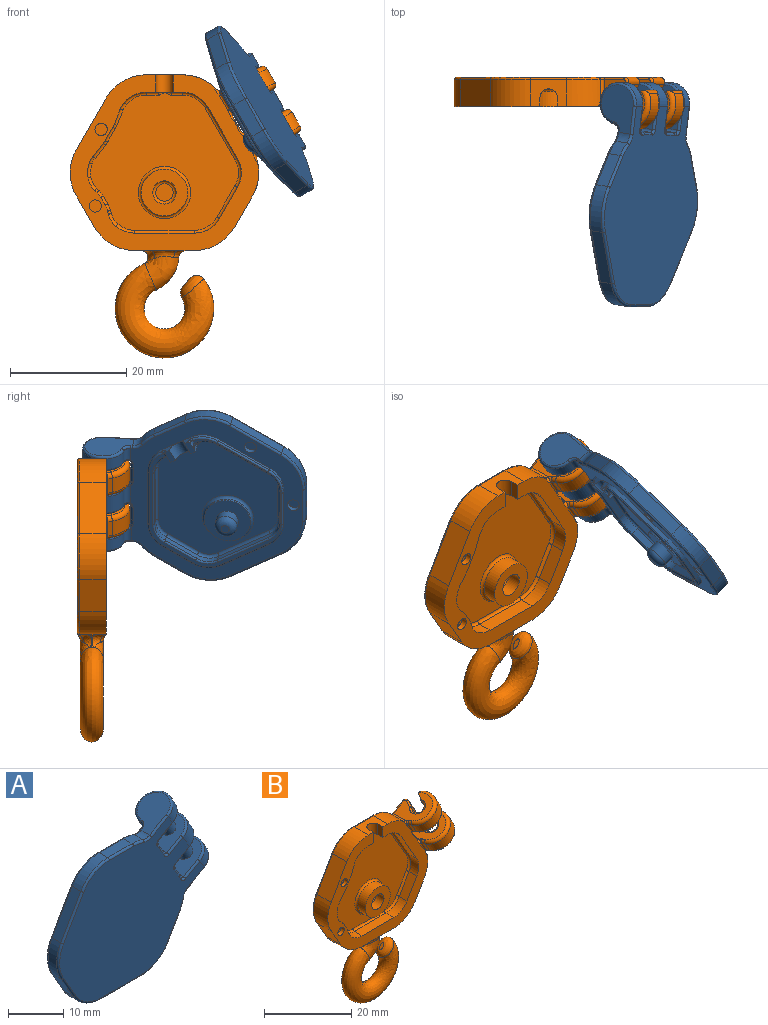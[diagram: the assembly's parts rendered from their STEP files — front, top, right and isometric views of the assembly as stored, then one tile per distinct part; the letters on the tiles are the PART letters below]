
ASSEMBLY  parts=2 mates=1
PART A: 201 faces, bbox 41.9x8.3x35.3 mm
  f0: plane 3.11x1.5mm, normal (0,0,1), area 2.3mm2, adj f20,f39,f76,f77,f115,f116
  f1: plane 22.85x20.65mm, normal (0,1,0), area 295.9mm2, adj f79,f82,f84,f85,f86,f87,f88,f89
  f2: plane 1.2x0.11mm, normal (0,0,-1), area 0.1mm2, adj f47,f80,f96,f130
  f3: cylinder r=8mm len=2.65mm, axis (0,1,0), area 6.2mm2, adj f10,f68,f163,f170
  f4: cylinder r=8mm len=2.1mm, axis (0,1,0), area 2mm2, adj f12,f65,f134,f180
  f5: cylinder r=1.5mm len=5.48mm, axis (0.5,0,-0.87), area 43.4mm2, adj f21,f28
  f6: plane 2.26x2.1mm, normal (0.87,0,0.5), area 5.5mm2, adj f11,f66,f138,f194
  f7: cylinder r=8mm len=6.93mm, axis (0,1,0), area 18.4mm2, adj f8,f18,f155,f162
  f8: plane 10.23x2.2mm, normal (0,0,-1), area 22.5mm2, adj f7,f9,f157,f164
  f9: cylinder r=8mm len=6.93mm, axis (0,1,0), area 18.4mm2, adj f8,f10,f159,f166
  f10: plane 5.39x3.11mm, normal (0.87,0,-0.5), area 13.7mm2, adj f3,f9,f161,f168
  f11: cylinder r=8mm len=2.1mm, axis (0,1,0), area 2mm2, adj f6,f67,f132,f195
  f12: plane 2.26x2.1mm, normal (0.87,0,0.5), area 5.5mm2, adj f4,f64,f136,f181
  f13: cylinder r=8mm len=2.78mm, axis (0,1,0), area 6.2mm2, adj f14,f69,f143,f150
  f14: plane 6.23x2.2mm, normal (0,0,1), area 13.7mm2, adj f13,f15,f145,f152
  f15: cylinder r=8mm len=6.93mm, axis (0,1,0), area 18.4mm2, adj f14,f16,f147,f154
  f16: plane 8.86x5.11mm, normal (-0.87,0,0.5), area 22.5mm2, adj f15,f17,f149,f156
  f17: cylinder r=8mm len=8mm, axis (0,1,0), area 18.4mm2, adj f16,f18,f151,f158
  f18: plane 5.39x3.11mm, normal (-0.87,0,-0.5), area 13.7mm2, adj f7,f17,f153,f160
  f19: plane 36.96x31.6mm, normal (0,-1,0), area 769.8mm2, adj f24,f27,f61,f140,f141,f143,f145,f147
  f20: plane 33.32x29.92mm, normal (0,1,0), area 251.9mm2, adj f0,f23,f26,f30,f31,f32,f33,f34
  f21: plane 6.4x6.34mm, normal (-0.5,0,0.87), area 29.7mm2, adj f5,f136,f137,f183,f184,f185
  f22: plane 6.4x6.34mm, normal (0.5,0,-0.87), area 29.7mm2, adj f25,f138,f139,f190,f191,f192
  f23: cylinder r=1.02mm len=3.53mm, axis (0.5,0,-0.87), area 4.9mm2, adj f20,f24,f185,f186,f189,f190
  f24: cylinder r=3.6mm len=7.82mm, axis (0.5,0,-0.87), area 53.2mm2, adj f19,f23,f184,f191
  f25: cylinder r=1.5mm len=5.48mm, axis (0.5,0,-0.87), area 43.4mm2, adj f22,f62
  f26: cylinder r=1.02mm len=2.42mm, axis (0.5,0,-0.87), area 3.2mm2, adj f20,f27,f144,f175,f176
  f27: cylinder r=3.6mm len=7.27mm, axis (0.5,0,-0.87), area 34.9mm2, adj f19,f26,f142,f177
  f28: plane 6.4x6.38mm, normal (0.5,0,-0.87), area 29.8mm2, adj f5,f134,f135,f176,f177,f178
  f29: plane 7.02x6.4mm, normal (-0.5,0,0.87), area 38.5mm2, adj f69,f140,f142,f144,f146
  f30: plane 9.65x0.7mm, normal (0,0,-1), area 6.8mm2, adj f20,f36,f41,f109
  f31: plane 5.39x3.11mm, normal (0.87,0,-0.5), area 4.4mm2, adj f20,f40,f41,f111
  f32: plane 8.86x5.11mm, normal (0.87,0,0.5), area 7.2mm2, adj f20,f39,f40,f113
  f33: plane 2.54x1.5mm, normal (0,0,1), area 1.9mm2, adj f20,f38,f76,f78,f102
  f34: plane 8.86x5.11mm, normal (-0.87,0,0.5), area 7.2mm2, adj f20,f37,f38,f105
  f35: plane 5.39x3.11mm, normal (-0.87,0,-0.5), area 4.4mm2, adj f20,f36,f37,f107
  f36: cylinder r=4.9mm len=4.24mm, axis (0,-1,0), area 3.6mm2, adj f20,f30,f35,f108
  f37: cylinder r=4.9mm len=4.9mm, axis (0,-1,0), area 3.6mm2, adj f20,f34,f35,f106
  f38: cylinder r=4.9mm len=4.24mm, axis (0,-1,0), area 3.6mm2, adj f20,f33,f34,f103,f104
  f39: cylinder r=4.9mm len=4.24mm, axis (0,-1,0), area 3.6mm2, adj f0,f20,f32,f114
  f40: cylinder r=4.9mm len=4.9mm, axis (0,-1,0), area 3.6mm2, adj f20,f31,f32,f112
  f41: cylinder r=4.9mm len=4.24mm, axis (0,-1,0), area 3.6mm2, adj f20,f30,f31,f110
  f42: plane 10.23x1.2mm, normal (0,0,1), area 12.3mm2, adj f43,f53,f90,f124
  f43: cylinder r=3.7mm len=3.2mm, axis (0,-1,0), area 4.6mm2, adj f42,f44,f91,f125
  f44: plane 5.39x3.11mm, normal (-0.87,0,0.5), area 7.5mm2, adj f43,f45,f92,f126
  f45: cylinder r=3.7mm len=3.7mm, axis (0,-1,0), area 4.6mm2, adj f44,f46,f93,f127
  f46: plane 8.86x5.11mm, normal (-0.87,0,-0.5), area 12.3mm2, adj f45,f47,f94,f128
  f47: cylinder r=3.7mm len=3.2mm, axis (0,-1,0), area 4.6mm2, adj f2,f46,f95,f129
  f48: plane 1.2x0.11mm, normal (0,0,-1), area 0.1mm2, adj f49,f81,f84,f118
  f49: cylinder r=3.7mm len=3.2mm, axis (0,-1,0), area 4.6mm2, adj f48,f50,f85,f119
  f50: plane 8.86x5.11mm, normal (0.87,0,-0.5), area 12.3mm2, adj f49,f51,f86,f120
  f51: cylinder r=3.7mm len=3.7mm, axis (0,-1,0), area 4.6mm2, adj f50,f52,f87,f121
  f52: plane 5.39x3.11mm, normal (0.87,0,0.5), area 7.5mm2, adj f51,f53,f88,f122
  f53: cylinder r=3.7mm len=3.2mm, axis (0,-1,0), area 4.6mm2, adj f42,f52,f89,f123
  f54: plane 25.08x23.45mm, normal (0,1,0), area 28.7mm2, adj f100,f101,f104,f105,f106,f107,f108,f109
  f55: cylinder r=4mm len=8mm, axis (0,-1,0), area 12.6mm2, adj f56,f99
  f56: plane 8x8mm, normal (0,1,0), area 38.9mm2, adj f55,f59
  f57: plane 1.4x1.4mm, normal (0,1,0), area 1.5mm2, adj f58
  f58: torus R=0.7mm, axis (0,1,0), area 17.3mm2, adj f57,f59
  f59: cylinder r=1.9mm len=3.8mm, axis (0,-1,0), area 21.5mm2, adj f56,f58
  f60: cylinder r=1.02mm len=2.61mm, axis (-0.5,0,0.87), area 3.5mm2, adj f20,f61,f171,f199,f200
  f61: cylinder r=3.6mm len=7.27mm, axis (-0.5,0,0.87), area 35mm2, adj f19,f60,f169,f198
  f62: plane 6.4x6.38mm, normal (-0.5,0,0.87), area 29.8mm2, adj f25,f132,f133,f197,f198,f199
  f63: plane 7.02x6.4mm, normal (0.5,0,-0.87), area 38.5mm2, adj f68,f167,f169,f171,f173
  f64: cylinder r=0.5mm len=2.51mm, axis (0.5,0,-0.87), area 2.1mm2, adj f12,f20,f65,f137
  f65: torus R=7.5mm, axis (0,1,0), area 0.8mm2, adj f4,f20,f64,f135
  f66: cylinder r=0.5mm len=2.51mm, axis (0.5,0,-0.87), area 2.1mm2, adj f6,f20,f67,f139
  f67: torus R=7.5mm, axis (0,1,0), area 0.8mm2, adj f11,f20,f66,f133
  f68: cylinder r=2mm len=2.2mm, axis (0,1,0), area 3.9mm2, adj f3,f63,f165,f172
  f69: cylinder r=2mm len=2.2mm, axis (0,1,0), area 3.9mm2, adj f13,f29,f141,f148
  f70: cylinder r=1.05mm len=2.1mm, axis (0,1,0), area 6.9mm2, adj f20,f71
  f71: plane 2.1x2.1mm, normal (0,1,0), area 3.5mm2, adj f70
  f72: cylinder r=1.05mm len=2.1mm, axis (0,1,0), area 6.9mm2, adj f20,f73
  f73: plane 2.1x2.1mm, normal (0,1,0), area 3.5mm2, adj f72
  f74: plane 2x0.5mm, normal (1,0,0), area 1mm2, adj f77,f79,f80,f98
  f75: plane 2x0.5mm, normal (-1,0,0), area 1mm2, adj f78,f79,f81,f82
  f76: cylinder r=1.5mm len=3mm, axis (0,0,-1), area 10.4mm2, adj f0,f33,f77,f78,f79
  f77: plane 2.2x1mm, normal (0,1,0), area 2.2mm2, adj f0,f74,f76,f79,f100,f116
  f78: plane 2.2x1mm, normal (0,1,0), area 2.2mm2, adj f33,f75,f76,f79,f101,f102
  f79: plane 6x2.5mm, normal (0,0,-1), area 9.1mm2, adj f1,f74,f75,f76,f77,f78,f82,f98
  f80: cylinder r=0.5mm len=2mm, axis (0,1,0), area 1.3mm2, adj f2,f74,f97,f131
  f81: cylinder r=0.5mm len=2mm, axis (0,-1,0), area 1.3mm2, adj f48,f75,f83,f117
  f82: cylinder r=0.5mm len=0.5mm, axis (0,0,-1), area 0.4mm2, adj f1,f75,f79,f83
  f83: sphere r=0.5mm, area 0.5mm2, adj f81,f82,f84
  f84: cylinder r=0.5mm len=0.5mm, axis (1,0,0), area 0.1mm2, adj f1,f48,f83,f85
  f85: torus R=3.2mm, axis (0,-1,0), area 2.9mm2, adj f1,f49,f84,f86
  f86: cylinder r=0.5mm len=9.11mm, axis (0.5,0,0.87), area 8mm2, adj f1,f50,f85,f87
  f87: torus R=3.2mm, axis (0,-1,0), area 2.9mm2, adj f1,f51,f86,f88
  f88: cylinder r=0.5mm len=5.64mm, axis (-0.5,0,0.87), area 4.9mm2, adj f1,f52,f87,f89
  f89: torus R=3.2mm, axis (0,-1,0), area 2.9mm2, adj f1,f53,f88,f90
  f90: cylinder r=0.5mm len=10.23mm, axis (-1,0,0), area 8mm2, adj f1,f42,f89,f91
  f91: torus R=3.2mm, axis (0,-1,0), area 2.9mm2, adj f1,f43,f90,f92
  f92: cylinder r=0.5mm len=5.64mm, axis (-0.5,0,-0.87), area 4.9mm2, adj f1,f44,f91,f93
  f93: torus R=3.2mm, axis (0,-1,0), area 2.9mm2, adj f1,f45,f92,f94
  f94: cylinder r=0.5mm len=9.11mm, axis (0.5,0,-0.87), area 8mm2, adj f1,f46,f93,f95
  f95: torus R=3.2mm, axis (0,-1,0), area 2.9mm2, adj f1,f47,f94,f96
  f96: cylinder r=0.5mm len=0.5mm, axis (1,0,0), area 0.1mm2, adj f1,f2,f95,f97
  f97: sphere r=0.5mm, area 0.4mm2, adj f80,f96,f98
  f98: cylinder r=0.5mm len=0.5mm, axis (0,0,-1), area 0.4mm2, adj f1,f74,f79,f97
  f99: torus R=4.5mm, axis (0,-1,0), area 20.6mm2, adj f1,f55
  f100: cylinder r=0.5mm len=1.4mm, axis (0,0,1), area 0.8mm2, adj f54,f77,f116,f131
  f101: cylinder r=0.5mm len=1.4mm, axis (0,0,-1), area 0.7mm2, adj f54,f78,f102,f103,f117
  f102: torus R=0.8mm, axis (0,0,1), area 0.3mm2, adj f33,f78,f101,f103
  f103: bspline ~0.69x0.47mm, area 0.2mm2, adj f38,f101,f102,f104
  f104: torus R=4.6mm, axis (0,1,0), area 2.1mm2, adj f38,f54,f103,f105
  f105: cylinder r=0.3mm len=9.01mm, axis (-0.5,0,-0.87), area 4.8mm2, adj f34,f54,f104,f106
  f106: torus R=4.6mm, axis (0,1,0), area 2.4mm2, adj f37,f54,f105,f107
  f107: cylinder r=0.3mm len=5.54mm, axis (0.5,0,-0.87), area 2.9mm2, adj f35,f54,f106,f108
  f108: torus R=4.6mm, axis (0,1,0), area 2.4mm2, adj f36,f54,f107,f109
  f109: cylinder r=0.3mm len=9.65mm, axis (1,0,0), area 4.5mm2, adj f30,f54,f108,f110
  f110: torus R=4.6mm, axis (0,1,0), area 2.4mm2, adj f41,f54,f109,f111
  f111: cylinder r=0.3mm len=5.54mm, axis (0.5,0,0.87), area 2.9mm2, adj f31,f54,f110,f112
  f112: torus R=4.6mm, axis (0,1,0), area 2.4mm2, adj f40,f54,f111,f113
  f113: cylinder r=0.3mm len=9.01mm, axis (-0.5,0,0.87), area 4.8mm2, adj f32,f54,f112,f114
  f114: torus R=4.6mm, axis (0,1,0), area 2.4mm2, adj f39,f54,f113,f115
  f115: cylinder r=0.3mm len=0.3mm, axis (-1,0,0), area 0.1mm2, adj f0,f54,f114,f116
  f116: torus R=0.8mm, axis (0,0,1), area 0.5mm2, adj f0,f77,f100,f115
  f117: bspline ~0.8x0.8mm, area 0.2mm2, adj f81,f101,f118
  f118: cylinder r=0.3mm len=0.3mm, axis (1,0,0), area 0.1mm2, adj f48,f54,f117,f119
  f119: torus R=4mm, axis (0,1,0), area 1.9mm2, adj f49,f54,f118,f120
  f120: cylinder r=0.3mm len=9.01mm, axis (0.5,0,0.87), area 4.8mm2, adj f50,f54,f119,f121
  f121: torus R=4mm, axis (0,1,0), area 1.9mm2, adj f51,f54,f120,f122
  f122: cylinder r=0.3mm len=5.54mm, axis (-0.5,0,0.87), area 2.9mm2, adj f52,f54,f121,f123
  f123: torus R=4mm, axis (0,1,0), area 1.9mm2, adj f53,f54,f122,f124
  f124: cylinder r=0.3mm len=10.23mm, axis (-1,0,0), area 4.8mm2, adj f42,f54,f123,f125
  f125: torus R=4mm, axis (0,1,0), area 1.9mm2, adj f43,f54,f124,f126
  f126: cylinder r=0.3mm len=5.54mm, axis (-0.5,0,-0.87), area 2.9mm2, adj f44,f54,f125,f127
  f127: torus R=4mm, axis (0,1,0), area 1.9mm2, adj f45,f54,f126,f128
  f128: cylinder r=0.3mm len=9.01mm, axis (0.5,0,-0.87), area 4.8mm2, adj f46,f54,f127,f129
  f129: torus R=4mm, axis (0,1,0), area 1.9mm2, adj f47,f54,f128,f130
  f130: cylinder r=0.3mm len=0.3mm, axis (1,0,0), area 0.1mm2, adj f2,f54,f129,f131
  f131: bspline ~0.8x0.8mm, area 0.2mm2, adj f80,f100,f130
  f132: cylinder r=0.5mm len=2.1mm, axis (0,1,0), area 1.8mm2, adj f11,f62,f133,f196
  f133: bspline ~1.19x1.14mm, area 0.3mm2, adj f20,f62,f67,f132,f200
  f134: cylinder r=0.5mm len=2.1mm, axis (0,1,0), area 1.8mm2, adj f4,f28,f135,f179
  f135: bspline ~1.14x1.02mm, area 0.2mm2, adj f28,f65,f134,f174,f175
  f136: cylinder r=0.5mm len=2.1mm, axis (0,1,0), area 1.6mm2, adj f12,f21,f137,f182
  f137: torus R=1mm, axis (-0.5,0,0.87), area 0.2mm2, adj f21,f64,f136,f186,f187
  f138: cylinder r=0.5mm len=2.1mm, axis (0,-1,0), area 1.6mm2, adj f6,f22,f139,f193
  f139: torus R=1mm, axis (-0.5,0,0.87), area 0.2mm2, adj f22,f66,f138,f188,f189
  f140: cylinder r=0.4mm len=4.45mm, axis (-0.87,0,-0.5), area 3.1mm2, adj f19,f29,f141,f142
  f141: torus R=2.4mm, axis (0,-1,0), area 1.2mm2, adj f19,f69,f140,f143
  f142: torus R=3.2mm, axis (-0.5,0,0.87), area 10mm2, adj f27,f29,f140,f144
  f143: torus R=7.6mm, axis (0,-1,0), area 1.7mm2, adj f13,f19,f141,f145
  f144: torus R=1.42mm, axis (-0.5,0,0.87), area 1.1mm2, adj f26,f29,f142,f146
  f145: cylinder r=0.4mm len=6.23mm, axis (1,0,0), area 3.9mm2, adj f14,f19,f143,f147
  f146: cylinder r=0.4mm len=0.5mm, axis (0.87,0,0.5), area 0.2mm2, adj f20,f29,f144,f148
  f147: torus R=7.6mm, axis (0,-1,0), area 5.2mm2, adj f15,f19,f145,f149
  f148: torus R=2.4mm, axis (0,1,0), area 1.2mm2, adj f20,f69,f146,f150
  f149: cylinder r=0.4mm len=9.06mm, axis (0.5,0,0.87), area 6.4mm2, adj f16,f19,f147,f151
  f150: torus R=7.6mm, axis (0,1,0), area 1.7mm2, adj f13,f20,f148,f152
  f151: torus R=7.6mm, axis (0,-1,0), area 5.2mm2, adj f17,f19,f149,f153
  f152: cylinder r=0.4mm len=6.23mm, axis (1,0,0), area 3.9mm2, adj f14,f20,f150,f154
  f153: cylinder r=0.4mm len=5.59mm, axis (-0.5,0,0.87), area 3.9mm2, adj f18,f19,f151,f155
  f154: torus R=7.6mm, axis (0,1,0), area 5.2mm2, adj f15,f20,f152,f156
  f155: torus R=7.6mm, axis (0,-1,0), area 5.2mm2, adj f7,f19,f153,f157
  f156: cylinder r=0.4mm len=9.06mm, axis (0.5,0,0.87), area 6.4mm2, adj f16,f20,f154,f158
  f157: cylinder r=0.4mm len=10.23mm, axis (-1,0,0), area 6.4mm2, adj f8,f19,f155,f159
  f158: torus R=7.6mm, axis (0,1,0), area 5.2mm2, adj f17,f20,f156,f160
  f159: torus R=7.6mm, axis (0,-1,0), area 5.2mm2, adj f9,f19,f157,f161
  f160: cylinder r=0.4mm len=5.59mm, axis (-0.5,0,0.87), area 3.9mm2, adj f18,f20,f158,f162
  f161: cylinder r=0.4mm len=5.59mm, axis (-0.5,0,-0.87), area 3.9mm2, adj f10,f19,f159,f163
  f162: torus R=7.6mm, axis (0,1,0), area 5.2mm2, adj f7,f20,f160,f164
  f163: torus R=7.6mm, axis (0,-1,0), area 1.7mm2, adj f3,f19,f161,f165
  f164: cylinder r=0.4mm len=10.23mm, axis (-1,0,0), area 6.4mm2, adj f8,f20,f162,f166
  f165: torus R=2.4mm, axis (0,-1,0), area 1.2mm2, adj f19,f68,f163,f167
  f166: torus R=7.6mm, axis (0,1,0), area 5.2mm2, adj f9,f20,f164,f168
  f167: cylinder r=0.4mm len=4.45mm, axis (-0.87,0,-0.5), area 3.1mm2, adj f19,f63,f165,f169
  f168: cylinder r=0.4mm len=5.59mm, axis (-0.5,0,-0.87), area 3.9mm2, adj f10,f20,f166,f170
  f169: torus R=3.2mm, axis (-0.5,0,0.87), area 10mm2, adj f61,f63,f167,f171
  f170: torus R=7.6mm, axis (0,1,0), area 1.7mm2, adj f3,f20,f168,f172
  f171: torus R=1.42mm, axis (-0.5,0,0.87), area 1.2mm2, adj f60,f63,f169,f173
  f172: torus R=2.4mm, axis (0,1,0), area 1.2mm2, adj f20,f68,f170,f173
  f173: cylinder r=0.4mm len=0.43mm, axis (0.87,0,0.5), area 0.1mm2, adj f20,f63,f171,f172
  f174: bspline ~0.97x0.49mm, area 0.2mm2, adj f20,f135,f175
  f175: bspline ~0.58x0.55mm, area 0.2mm2, adj f26,f135,f174,f176
  f176: torus R=1.42mm, axis (-0.5,0,0.87), area 0.9mm2, adj f26,f28,f175,f177
  f177: torus R=3.2mm, axis (-0.5,0,0.87), area 10mm2, adj f27,f28,f176,f178
  f178: cylinder r=0.4mm len=3.8mm, axis (0.87,0,0.5), area 2.6mm2, adj f19,f28,f177,f179
  f179: torus R=0.9mm, axis (0,-1,0), area 0.7mm2, adj f19,f134,f178,f180
  f180: torus R=7.6mm, axis (0,-1,0), area 0.6mm2, adj f4,f19,f179,f181
  f181: cylinder r=0.4mm len=2.46mm, axis (0.5,0,-0.87), area 1.6mm2, adj f12,f19,f180,f182
  f182: torus R=0.9mm, axis (0,-1,0), area 0.6mm2, adj f19,f136,f181,f183
  f183: cylinder r=0.4mm len=3.75mm, axis (-0.87,0,-0.5), area 2.6mm2, adj f19,f21,f182,f184
  f184: torus R=3.2mm, axis (-0.5,0,0.87), area 10mm2, adj f21,f24,f183,f185
  f185: torus R=1.42mm, axis (-0.5,0,0.87), area 0.8mm2, adj f21,f23,f184,f186
  f186: bspline ~0.53x0.49mm, area 0.2mm2, adj f23,f137,f185,f187
  f187: bspline ~1x0.46mm, area 0.2mm2, adj f20,f137,f186
  f188: bspline ~1.06x0.52mm, area 0.2mm2, adj f20,f139,f189
  f189: bspline ~0.59x0.56mm, area 0.2mm2, adj f23,f139,f188,f190
  f190: torus R=1.42mm, axis (-0.5,0,0.87), area 0.8mm2, adj f22,f23,f189,f191
  f191: torus R=3.2mm, axis (-0.5,0,0.87), area 10mm2, adj f22,f24,f190,f192
  f192: cylinder r=0.4mm len=3.75mm, axis (0.87,0,0.5), area 2.6mm2, adj f19,f22,f191,f193
  f193: torus R=0.9mm, axis (0,-1,0), area 0.6mm2, adj f19,f138,f192,f194
  f194: cylinder r=0.4mm len=2.46mm, axis (0.5,0,-0.87), area 1.6mm2, adj f6,f19,f193,f195
  f195: torus R=7.6mm, axis (0,-1,0), area 0.6mm2, adj f11,f19,f194,f196
  f196: torus R=0.9mm, axis (0,-1,0), area 0.7mm2, adj f19,f132,f195,f197
  f197: cylinder r=0.4mm len=3.8mm, axis (-0.87,0,-0.5), area 2.6mm2, adj f19,f62,f196,f198
  f198: torus R=3.2mm, axis (-0.5,0,0.87), area 10mm2, adj f61,f62,f197,f199
  f199: torus R=1.42mm, axis (-0.5,0,0.87), area 0.9mm2, adj f60,f62,f198,f200
  f200: bspline ~1.01x0.53mm, area 0.3mm2, adj f20,f60,f133,f199
PART B: 175 faces, bbox 40.8x9.9x50.5 mm
  f0: plane 25.59x23.89mm, normal (0,-1,0), area 389.1mm2, adj f86,f148,f149,f150,f151,f152,f153,f154
  f1: bspline ~5.44x2.72mm, area 0.9mm2, adj f33,f40,f91,f93
  f2: plane 4.61x2.81mm, normal (0,0,-1), area 8.2mm2, adj f16,f37,f88,f103
  f3: cylinder r=0.4mm len=0.64mm, axis (0.5,0,-0.87), area 0.1mm2, adj f16,f59,f78,f82
  f4: cylinder r=0.4mm len=2.95mm, axis (0.5,0,-0.87), area 1.4mm2, adj f16,f54,f70,f71,f82,f83
  f5: plane 35.08x29.66mm, normal (0,1,0), area 762.7mm2, adj f13,f57,f98,f99,f100,f101,f102,f103
  f6: cylinder r=1.55mm len=4.67mm, axis (-0.5,0,0.87), area 23.3mm2, adj f7,f14,f120,f133
  f7: plane 4.38x3.19mm, normal (-0.72,0.55,-0.42), area 9.4mm2, adj f6,f12,f50,f60,f120,f133
  f8: cylinder r=4.5mm len=8.97mm, axis (-0.5,0,0.87), area 40.3mm2, adj f9,f12,f77,f81
  f9: plane 2.56x1.63mm, normal (-0.82,-0.34,-0.47), area 2.2mm2, adj f8,f11,f76,f80
  f10: plane 3.56x2.56mm, normal (0.77,-0.45,0.45), area 7.1mm2, adj f13,f14,f118,f131
  f11: cylinder r=0.4mm len=2.95mm, axis (0.5,0,-0.87), area 1.4mm2, adj f9,f16,f74,f75,f78,f79
  f12: cylinder r=0.8mm len=4.51mm, axis (-0.5,0,0.87), area 6.5mm2, adj f7,f8,f50,f60,f77,f81
  f13: cylinder r=0.8mm len=3.52mm, axis (-0.5,0,0.87), area 5.9mm2, adj f5,f10,f117,f130
  f14: cylinder r=0.8mm len=3.25mm, axis (-0.5,0,0.87), area 1.5mm2, adj f6,f10,f119,f132
  f15: cylinder r=8mm len=5.82mm, axis (0,1,0), area 29.8mm2, adj f16,f27,f65,f74,f114
  f16: plane 32.67x30.47mm, normal (0,-1,0), area 255.9mm2, adj f2,f3,f4,f11,f15,f17,f18,f19
  f17: plane 2.5x2.04mm, normal (0,0,-1), area 4.3mm2, adj f16,f21,f46,f48,f164
  f18: plane 2.5x1.95mm, normal (0,0,-1), area 4mm2, adj f16,f22,f46,f47,f149
  f19: cylinder r=5mm len=3.24mm, axis (0,1,0), area 8.8mm2, adj f16,f34,f144,f156
  f20: cylinder r=5mm len=2.6mm, axis (0,1,0), area 6.6mm2, adj f16,f145,f146,f167
  f21: cylinder r=5mm len=3.82mm, axis (0,1,0), area 10.9mm2, adj f16,f17,f147,f166
  f22: cylinder r=5mm len=4.33mm, axis (0,1,0), area 13.1mm2, adj f16,f18,f35,f150
  f23: cylinder r=5mm len=5mm, axis (0,1,0), area 13.1mm2, adj f16,f35,f36,f152
  f24: cylinder r=5mm len=4.33mm, axis (0,1,0), area 13.1mm2, adj f16,f34,f36,f154
  f25: plane 5.39x4.6mm, normal (0.87,0,-0.5), area 28.6mm2, adj f16,f26,f37,f101
  f26: cylinder r=8mm len=6.29mm, axis (0,1,0), area 29.8mm2, adj f16,f25,f64,f70,f100
  f27: plane 6.23x4.6mm, normal (0,0,1), area 20.6mm2, adj f15,f16,f28,f46,f47,f48,f113
  f28: cylinder r=8mm len=6.93mm, axis (0,1,0), area 38.5mm2, adj f16,f27,f29,f112
  f29: plane 8.86x5.11mm, normal (-0.87,0,0.5), area 47mm2, adj f16,f28,f30,f111
  f30: cylinder r=8mm len=8mm, axis (0,1,0), area 38.5mm2, adj f16,f29,f31,f110
  f31: plane 5.39x4.6mm, normal (-0.87,0,-0.5), area 28.6mm2, adj f16,f30,f32,f109
  f32: cylinder r=8mm len=6.93mm, axis (0,1,0), area 38.5mm2, adj f16,f31,f33,f108
  f33: plane 4.61x2.76mm, normal (0,0,-1), area 7.3mm2, adj f1,f16,f32,f91,f92,f93,f107
  f34: plane 10.23x2.5mm, normal (0,0,1), area 25.6mm2, adj f16,f19,f24,f155
  f35: plane 8.86x5.11mm, normal (-0.87,0,-0.5), area 25.6mm2, adj f16,f22,f23,f151
  f36: plane 5.39x3.11mm, normal (-0.87,0,0.5), area 15.6mm2, adj f16,f23,f24,f153
  f37: cylinder r=8mm len=6.93mm, axis (0,1,0), area 38.5mm2, adj f2,f16,f25,f102
  f38: plane 1.51x1.27mm, normal (-0.77,0,0.64), area 1.3mm2, adj f41
  f39: bspline ~5.85x5.85mm, area 56.1mm2, adj f40,f88,f89,f90,f91,f92
  f40: bspline ~16.91x16.22mm, area 418.7mm2, adj f1,f39,f41,f93
  f41: bspline ~4.82x4.42mm, area 27.9mm2, adj f38,f40
  f42: plane 8x8mm, normal (0,-1,0), area 37.7mm2, adj f43,f44
  f43: cylinder r=2mm len=4mm, axis (0,1,0), area 31.4mm2, adj f42,f87
  f44: cylinder r=4mm len=8mm, axis (0,1,0), area 62.8mm2, adj f42,f86
  f45: plane 3x3mm, normal (0,-1,0), area 7.1mm2, adj f87
  f46: cylinder r=1.5mm len=3mm, axis (0,0,1), area 14.1mm2, adj f17,f18,f27,f47,f48,f148,f162
  f47: plane 3x1.5mm, normal (-1,0,0), area 4.5mm2, adj f16,f18,f27,f46
  f48: plane 3x1.5mm, normal (1,0,0), area 4.5mm2, adj f16,f17,f27,f46
  f49: plane 7.8x6.87mm, normal (0.5,0,-0.87), area 31.7mm2, adj f52,f56,f64,f71,f72,f73,f94,f95
  f50: plane 7.8x6.87mm, normal (-0.5,0,0.87), area 31.7mm2, adj f7,f12,f65,f75,f76,f77,f116,f117
  f51: cylinder r=1.55mm len=4.67mm, axis (-0.5,0,0.87), area 23.3mm2, adj f52,f58,f94,f121
  f52: plane 4.38x3.19mm, normal (-0.72,0.55,-0.42), area 9.4mm2, adj f49,f51,f56,f61,f94,f121
  f53: cylinder r=4.5mm len=8.97mm, axis (-0.5,0,0.87), area 40.3mm2, adj f54,f56,f73,f85
  f54: plane 2.56x1.63mm, normal (-0.82,-0.34,-0.47), area 2.2mm2, adj f4,f53,f72,f84
  f55: plane 3.56x2.56mm, normal (0.77,-0.45,0.45), area 7.1mm2, adj f57,f58,f96,f123
  f56: cylinder r=0.8mm len=4.51mm, axis (-0.5,0,0.87), area 6.5mm2, adj f49,f52,f53,f61,f73,f85
  f57: cylinder r=0.8mm len=3.52mm, axis (-0.5,0,0.87), area 5.9mm2, adj f5,f55,f97,f124
  f58: cylinder r=0.8mm len=3.25mm, axis (-0.5,0,0.87), area 1.5mm2, adj f51,f55,f95,f122
  f59: plane 4.87x2.84mm, normal (0.87,0,0.5), area 13.3mm2, adj f3,f62,f63,f78,f82,f127
  f60: plane 7.8x6.77mm, normal (0.5,0,-0.87), area 31.3mm2, adj f7,f12,f63,f79,f80,f81,f129,f130
  f61: plane 7.8x6.77mm, normal (-0.5,0,0.87), area 31.3mm2, adj f52,f56,f62,f83,f84,f85,f121,f122
  f62: cylinder r=0.6mm len=4.07mm, axis (0,-1,0), area 3.8mm2, adj f59,f61,f82,f126
  f63: cylinder r=0.6mm len=4.07mm, axis (0,1,0), area 3.8mm2, adj f59,f60,f78,f128
  f64: cylinder r=0.6mm len=4.03mm, axis (0,1,0), area 3.2mm2, adj f26,f49,f70,f99
  f65: cylinder r=0.6mm len=4.03mm, axis (0,1,0), area 3.2mm2, adj f15,f50,f74,f115
  f66: cylinder r=1.05mm len=2.1mm, axis (0,-1,0), area 6.9mm2, adj f16,f67
  f67: plane 2.1x2.1mm, normal (0,-1,0), area 3.5mm2, adj f66
  f68: cylinder r=1.05mm len=2.1mm, axis (0,-1,0), area 6.9mm2, adj f16,f69
  f69: plane 2.1x2.1mm, normal (0,-1,0), area 3.5mm2, adj f68
  f70: bspline ~2.03x0.99mm, area 1.1mm2, adj f4,f16,f26,f64,f71
  f71: torus R=1.2mm, axis (0.5,0,-0.87), area 0.6mm2, adj f4,f49,f70,f72
  f72: cylinder r=0.8mm len=1.28mm, axis (0.29,-0.94,0.17), area 1mm2, adj f49,f54,f71,f73
  f73: torus R=3.7mm, axis (0.5,0,-0.87), area 17.5mm2, adj f49,f53,f56,f72
  f74: bspline ~1.62x1.44mm, area 1.1mm2, adj f11,f15,f16,f65,f75
  f75: torus R=1.2mm, axis (0.5,0,-0.87), area 0.6mm2, adj f11,f50,f74,f76
  f76: cylinder r=0.8mm len=1.2mm, axis (-0.29,0.94,-0.17), area 1mm2, adj f9,f50,f75,f77
  f77: torus R=3.7mm, axis (0.5,0,-0.87), area 17.5mm2, adj f8,f12,f50,f76
  f78: bspline ~2.46x1.48mm, area 1.6mm2, adj f3,f11,f16,f59,f63,f79
  f79: torus R=1.2mm, axis (0.5,0,-0.87), area 0.5mm2, adj f11,f60,f78,f80
  f80: cylinder r=0.8mm len=1.28mm, axis (0.29,-0.94,0.17), area 1mm2, adj f9,f60,f79,f81
  f81: torus R=3.7mm, axis (0.5,0,-0.87), area 17.5mm2, adj f8,f12,f60,f80
  f82: bspline ~2.41x1.59mm, area 1.6mm2, adj f3,f4,f16,f59,f62,f83
  f83: torus R=1.2mm, axis (0.5,0,-0.87), area 0.5mm2, adj f4,f61,f82,f84
  f84: cylinder r=0.8mm len=1.2mm, axis (-0.29,0.94,-0.17), area 1mm2, adj f54,f61,f83,f85
  f85: torus R=3.7mm, axis (0.5,0,-0.87), area 17.5mm2, adj f53,f56,f61,f84
  f86: torus R=4.5mm, axis (0,-1,0), area 20.6mm2, adj f0,f44
  f87: torus R=1.5mm, axis (0,-1,0), area 9mm2, adj f43,f45
  f88: bspline ~5.47x2.47mm, area 8.1mm2, adj f2,f39,f89,f90,f104
  f89: bspline ~5.06x1.5mm, area 5.4mm2, adj f16,f39,f88,f91
  f90: bspline ~5.15x1.53mm, area 4.2mm2, adj f39,f88,f92,f105
  f91: bspline ~4.67x4.13mm, area 4.9mm2, adj f1,f33,f39,f89
  f92: bspline ~2.43x2.26mm, area 4.8mm2, adj f33,f39,f90,f93,f106
  f93: bspline ~5.44x2.72mm, area 0.9mm2, adj f1,f33,f40,f92
  f94: torus R=1.95mm, axis (0.5,0,-0.87), area 4.6mm2, adj f49,f51,f52,f95
  f95: torus R=0.4mm, axis (0.5,0,-0.87), area 0.2mm2, adj f49,f58,f94,f96
  f96: cylinder r=0.4mm len=1.93mm, axis (0.39,0.89,0.22), area 1.2mm2, adj f49,f55,f95,f97
  f97: torus R=0.4mm, axis (0.5,0,-0.87), area 0.8mm2, adj f49,f57,f96,f98
  f98: cylinder r=0.4mm len=3.49mm, axis (-0.87,0,-0.5), area 2.4mm2, adj f5,f49,f97,f99
  f99: torus R=1mm, axis (0,-1,0), area 0.6mm2, adj f5,f64,f98,f100
  f100: torus R=7.6mm, axis (0,-1,0), area 4mm2, adj f5,f26,f99,f101
  f101: cylinder r=0.4mm len=5.59mm, axis (0.5,0,0.87), area 3.9mm2, adj f5,f25,f100,f102
  f102: torus R=7.6mm, axis (0,-1,0), area 5.2mm2, adj f5,f37,f101,f103
  f103: cylinder r=0.4mm len=2.32mm, axis (1,0,0), area 1.5mm2, adj f2,f5,f102,f104
  f104: bspline ~1.82x0.54mm, area 0.4mm2, adj f5,f88,f103,f105
  f105: bspline ~4.41x0.44mm, area 1.6mm2, adj f5,f90,f104,f106
  f106: bspline ~2.07x0.58mm, area 0.4mm2, adj f5,f92,f105,f107
  f107: cylinder r=0.4mm len=2.26mm, axis (1,0,0), area 1.4mm2, adj f5,f33,f106,f108
  f108: torus R=7.6mm, axis (0,-1,0), area 5.2mm2, adj f5,f32,f107,f109
  f109: cylinder r=0.4mm len=5.59mm, axis (0.5,0,-0.87), area 3.9mm2, adj f5,f31,f108,f110
  f110: torus R=7.6mm, axis (0,-1,0), area 5.2mm2, adj f5,f30,f109,f111
  f111: cylinder r=0.4mm len=9.06mm, axis (-0.5,0,-0.87), area 6.4mm2, adj f5,f29,f110,f112
  f112: torus R=7.6mm, axis (0,-1,0), area 5.2mm2, adj f5,f28,f111,f113
  f113: cylinder r=0.4mm len=6.23mm, axis (-1,0,0), area 3.9mm2, adj f5,f27,f112,f114
  f114: torus R=7.6mm, axis (0,-1,0), area 4mm2, adj f5,f15,f113,f115
  f115: torus R=1mm, axis (0,-1,0), area 0.6mm2, adj f5,f65,f114,f116
  f116: cylinder r=0.4mm len=3.49mm, axis (0.87,0,0.5), area 2.4mm2, adj f5,f50,f115,f117
  f117: torus R=0.4mm, axis (0.5,0,-0.87), area 0.8mm2, adj f13,f50,f116,f118
  f118: cylinder r=0.4mm len=1.93mm, axis (-0.39,-0.89,-0.22), area 1.2mm2, adj f10,f50,f117,f119
  f119: torus R=0.4mm, axis (0.5,0,-0.87), area 0.2mm2, adj f14,f50,f118,f120
  f120: torus R=1.95mm, axis (0.5,0,-0.87), area 4.6mm2, adj f6,f7,f50,f119
  f121: torus R=1.95mm, axis (0.5,0,-0.87), area 4.6mm2, adj f51,f52,f61,f122
  f122: torus R=0.4mm, axis (0.5,0,-0.87), area 0.2mm2, adj f58,f61,f121,f123
  f123: cylinder r=0.4mm len=1.93mm, axis (-0.39,-0.89,-0.22), area 1.2mm2, adj f55,f61,f122,f124
  f124: torus R=0.4mm, axis (0.5,0,-0.87), area 0.8mm2, adj f57,f61,f123,f125
  f125: cylinder r=0.4mm len=3.39mm, axis (-0.87,0,-0.5), area 2.3mm2, adj f5,f61,f124,f126
  f126: torus R=1mm, axis (0,-1,0), area 0.7mm2, adj f5,f62,f125,f127
  f127: cylinder r=0.4mm len=2.8mm, axis (0.5,0,-0.87), area 1.9mm2, adj f5,f59,f126,f128
  f128: torus R=1mm, axis (0,-1,0), area 0.7mm2, adj f5,f63,f127,f129
  f129: cylinder r=0.4mm len=3.39mm, axis (0.87,0,0.5), area 2.3mm2, adj f5,f60,f128,f130
  f130: torus R=0.4mm, axis (0.5,0,-0.87), area 0.8mm2, adj f13,f60,f129,f131
  f131: cylinder r=0.4mm len=1.93mm, axis (0.39,0.89,0.22), area 1.2mm2, adj f10,f60,f130,f132
  f132: torus R=0.4mm, axis (0.5,0,-0.87), area 0.2mm2, adj f14,f60,f131,f133
  f133: torus R=1.95mm, axis (0.5,0,-0.87), area 4.6mm2, adj f6,f7,f60,f132
  f134: plane 2.5x1.33mm, normal (0.87,0,0.5), area 3.8mm2, adj f16,f142,f143,f160
  f135: plane 2.5x2.3mm, normal (0.87,0,-0.5), area 6.6mm2, adj f16,f140,f141,f174
  f136: plane 2.5x0.54mm, normal (0.97,0,0.25), area 1.4mm2, adj f16,f142,f144,f158
  f137: plane 2.5x0.4mm, normal (0.7,0,0.71), area 1.4mm2, adj f16,f143,f145,f163
  f138: plane 2.5x2.25mm, normal (0.79,0,-0.62), area 7.1mm2, adj f16,f140,f146,f171
  f139: plane 2.65x2.5mm, normal (0.93,0,-0.37), area 7.1mm2, adj f16,f141,f147,f170
  f140: cylinder r=4mm len=2.5mm, axis (0,-1,0), area 1.4mm2, adj f16,f135,f138,f173
  f141: cylinder r=4mm len=2.5mm, axis (0,-1,0), area 1.4mm2, adj f16,f135,f139,f172
  f142: cylinder r=4mm len=2.5mm, axis (0,-1,0), area 2.7mm2, adj f16,f134,f136,f159
  f143: cylinder r=4mm len=2.5mm, axis (0,-1,0), area 2.7mm2, adj f16,f134,f137,f161
  f144: cylinder r=4mm len=2.5mm, axis (0,1,0), area 6.1mm2, adj f16,f19,f136,f157
  f145: cylinder r=4mm len=2.5mm, axis (0,1,0), area 6.1mm2, adj f16,f20,f137,f165
  f146: cylinder r=4mm len=2.5mm, axis (0,1,0), area 3.2mm2, adj f16,f20,f138,f169
  f147: cylinder r=4mm len=2.5mm, axis (0,1,0), area 3.2mm2, adj f16,f21,f139,f168
  f148: bspline ~1.12x0.5mm, area 0.3mm2, adj f0,f46,f149
  f149: cylinder r=0.5mm len=1.95mm, axis (-1,0,0), area 1.5mm2, adj f0,f18,f148,f150
  f150: torus R=4.5mm, axis (0,-1,0), area 4mm2, adj f0,f22,f149,f151
  f151: cylinder r=0.5mm len=9.11mm, axis (-0.5,0,0.87), area 8mm2, adj f0,f35,f150,f152
  f152: torus R=4.5mm, axis (0,-1,0), area 4mm2, adj f0,f23,f151,f153
  f153: cylinder r=0.5mm len=5.64mm, axis (0.5,0,0.87), area 4.9mm2, adj f0,f36,f152,f154
  f154: torus R=4.5mm, axis (0,-1,0), area 4mm2, adj f0,f24,f153,f155
  f155: cylinder r=0.5mm len=10.23mm, axis (1,0,0), area 8mm2, adj f0,f34,f154,f156
  f156: torus R=4.5mm, axis (0,-1,0), area 2.7mm2, adj f0,f19,f155,f157
  f157: torus R=3.5mm, axis (0,-1,0), area 1.8mm2, adj f0,f144,f156,f158
  f158: cylinder r=0.5mm len=0.67mm, axis (0.25,0,-0.97), area 0.4mm2, adj f0,f136,f157,f159
  f159: torus R=4.5mm, axis (0,-1,0), area 0.9mm2, adj f0,f142,f158,f160
  f160: cylinder r=0.5mm len=1.58mm, axis (0.5,0,-0.87), area 1.2mm2, adj f0,f134,f159,f161
  f161: torus R=4.5mm, axis (0,-1,0), area 0.9mm2, adj f0,f143,f160,f163
  f162: bspline ~1.12x0.5mm, area 0.3mm2, adj f0,f46,f164
  f163: cylinder r=0.5mm len=0.75mm, axis (-0.71,0,0.7), area 0.4mm2, adj f0,f137,f161,f165
  f164: cylinder r=0.5mm len=2.04mm, axis (-1,0,0), area 1.6mm2, adj f0,f17,f162,f166
  f165: torus R=3.5mm, axis (0,-1,0), area 1.8mm2, adj f0,f145,f163,f167
  f166: torus R=4.5mm, axis (0,-1,0), area 3.3mm2, adj f0,f21,f164,f168
  f167: torus R=4.5mm, axis (0,-1,0), area 2mm2, adj f0,f20,f165,f169
  f168: torus R=3.5mm, axis (0,-1,0), area 1mm2, adj f0,f147,f166,f170
  f169: torus R=3.5mm, axis (0,-1,0), area 1mm2, adj f0,f146,f167,f171
  f170: cylinder r=0.5mm len=2.84mm, axis (0.37,0,0.93), area 2.2mm2, adj f0,f139,f168,f172
  f171: cylinder r=0.5mm len=2.56mm, axis (-0.62,0,-0.79), area 2.2mm2, adj f0,f138,f169,f173
  f172: torus R=4.5mm, axis (0,-1,0), area 0.5mm2, adj f0,f141,f170,f174
  f173: torus R=4.5mm, axis (0,-1,0), area 0.5mm2, adj f0,f140,f171,f174
  f174: cylinder r=0.5mm len=2.55mm, axis (0.5,0,0.87), area 2.1mm2, adj f0,f135,f172,f173
PLACE A rot(axis=(-0.5,0,0.87),82.5deg) t=(20.12,-29.41,11.62)mm
PLACE B at identity fixed
MATE revolute B.f77 <-> A.f24  axis (-0.5,0,0.87) through (16.58,-4.5,21.12)mm
